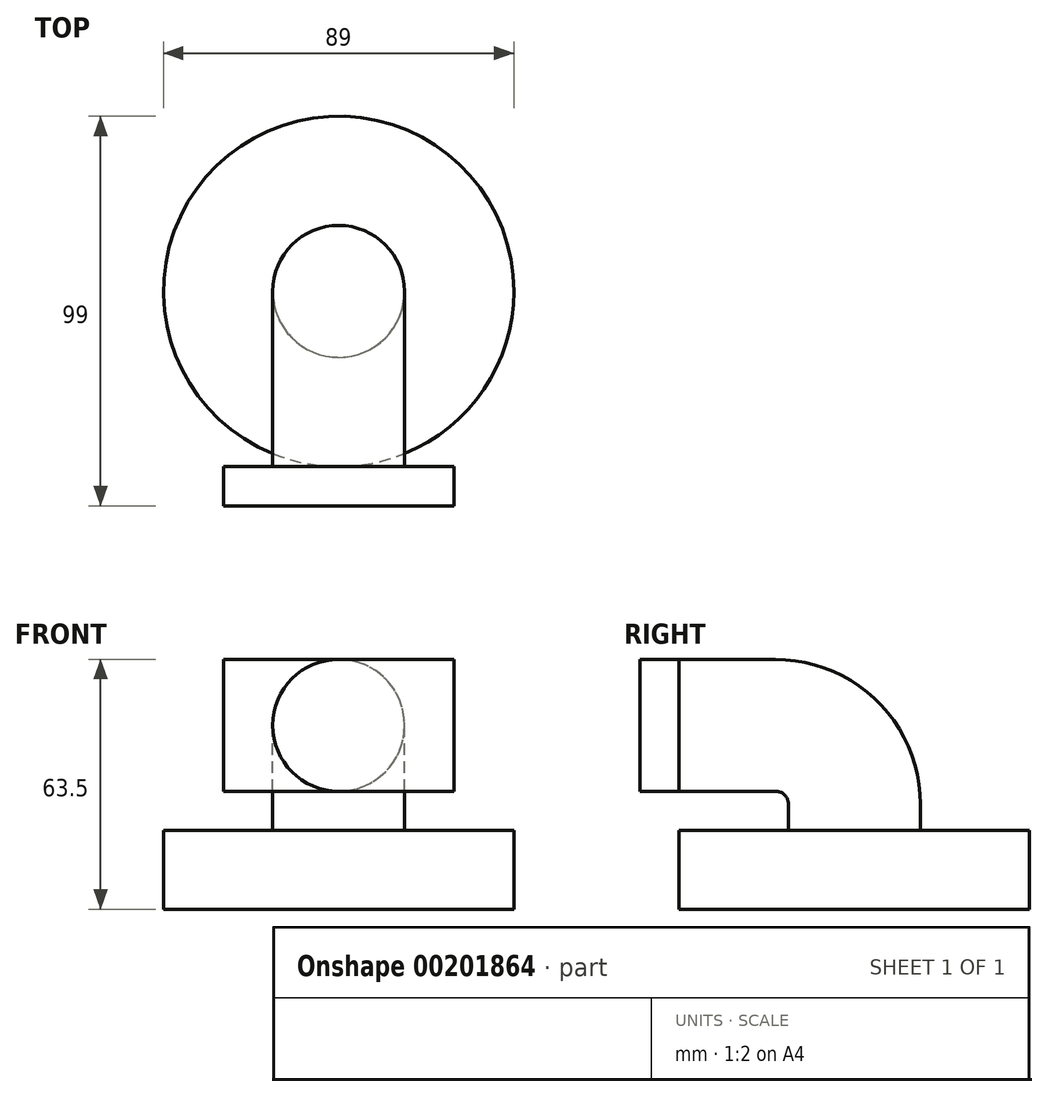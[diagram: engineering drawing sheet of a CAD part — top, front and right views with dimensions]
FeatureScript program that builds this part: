
annotation { "Feature Type Name" : "Feature", "Feature Type Description" : "" }
export const myFeature = defineFeature(function(context is Context, id is Id, definition is map)
    precondition{}
    {
        {
            var Q0;
            Q0=qCreatedBy(makeId("Top.planeOp"),FACE);
            var sketch = newSketch(context, id + "F0", { "sketchPlane" : qUnion([Q0])});
            skCircle(sketch, "E0", {"center": v(0, 0) * mm, "radius": 44.5 * mm});
            skSolve(sketch);
        }
        {
            var Q0;
            Q0=makeQuery(id+"F0.imprint","IMPRINT",FACE,{"disambiguationData":[TD([[makeQuery(id+"F0.imprint","IMPRINT",EDGE,{"derivedFrom":sQuery(id+"F0.wireOp",EDGE,"E0")}),1.0]])]});
            extrude(context, id + "F1", {"entities" : qUnion([Q0]), "depth" : 20 * mm, "offsetDistance" : 25 * mm});
        }
        {
            var Q0;
            Q0=qCreatedBy(makeId("Front.planeOp"),FACE);
            cPlane(context, id + "F2", {"entities" : qUnion([Q0]), "cplaneType" : CPlaneType.OFFSET, "offset" : (89 / 2) * mm, "width" : 150 * mm, "height" : 150 * mm});
        }
        {
            var Q0;
            Q0=makeQuery(id+"F1.opExtrude","CAP_FACE",FACE,{"disambiguationData":[OSD([sQuery(id+"F0.wireOp",EDGE,"E0")])],"isStart":false});
            var sketch = newSketch(context, id + "F3", { "sketchPlane" : qUnion([Q0])});
            skPoint(sketch, "E1", {"position": v(0, -44.5) * mm});
            skSolve(sketch);
        }
        {
            var Q0;
            Q0=qCreatedBy(id+"F2.planeOp",FACE);
            var sketch = newSketch(context, id + "F4", { "sketchPlane" : qUnion([Q0])});
            skLineSegment(sketch, "E2.bottom", {"start": v(29.25, 30) * mm, "end": v(-29.25, 30) * mm});
            skLineSegment(sketch, "E2.top", {"start": v(29.25, 63.5) * mm, "end": v(-29.25, 63.5) * mm});
            skLineSegment(sketch, "E2.left", {"start": v(29.25, 30) * mm, "end": v(29.25, 63.5) * mm});
            skLineSegment(sketch, "E2.right", {"start": v(-29.25, 30) * mm, "end": v(-29.25, 63.5) * mm});
            skPoint(sketch, "E2.middle", {"position": v(0, 46.75) * mm});
            skSolve(sketch);
        }
        {
            var Q0;
            Q0 = qSketchRegion(id + "F4", true);
            extrude(context, id + "F5", {"entities" : qUnion([Q0]), "depth" : 10 * mm, "offsetDistance" : 25 * mm});
        }
        {
            var Q0;
            Q0=makeQuery(id+"F3.imprint","IMPRINT",FACE,{"disambiguationData":[TD([[makeQuery(id+"F3.imprint","IMPRINT",EDGE,{"derivedFrom":makeQuery(id+"F1.opExtrude","CAP_EDGE",EDGE,{"disambiguationData":[OSD([sQuery(id+"F0.wireOp",EDGE,"E0")])],"isStart":false})}),1.0]])]});
            var sketch = newSketch(context, id + "F6", { "sketchPlane" : qUnion([Q0])});
            skPoint(sketch, "E3", {"position": v(0, 0) * mm});
            skSolve(sketch);
        }
        {
            var Q0;
            Q0=makeQuery(id+"F5.opExtrude","CAP_FACE",FACE,{"disambiguationData":[OSD([sQuery(id+"F4.wireOp",EDGE,"E2.bottom"),sQuery(id+"F4.wireOp",EDGE,"E2.top"),sQuery(id+"F4.wireOp",EDGE,"E2.left"),sQuery(id+"F4.wireOp",EDGE,"E2.right")])],"isStart":true});
            var sketch = newSketch(context, id + "F7", { "sketchPlane" : qUnion([Q0])});
            skCircle(sketch, "E4", {"center": v(0, 46.75) * mm, "radius": 16.75 * mm});
            skPoint(sketch, "E4.centerSnap0", {"position": v(29.25, 46.75) * mm});
            skPoint(sketch, "E4.centerSnap1", {"position": v(0, 63.5) * mm});
            skSolve(sketch);
        }
        {
            var Q0;
            Q0=qCreatedBy(makeId("Right.planeOp"),FACE);
            var sketch = newSketch(context, id + "F8", { "sketchPlane" : qUnion([Q0])});
            skPoint(sketch, "E5.0", {"position": v(-44.5, 46.75) * mm});
            skLineSegment(sketch, "E6", {"start": v(-44.5, 46.75) * mm, "end": v(-20, 46.75) * mm});
            skPoint(sketch, "E7.visualSharp", {"position": v(0, 46.75) * mm});
            skArc(sketch, "E7.filletArc", {"start": v(0, 26.75) * mm, "mid": v(-5.86, 40.9) * mm, "end": v(-20, 46.75) * mm});
            skPoint(sketch, "E8.0", {"position": v(0, 20) * mm});
            skLineSegment(sketch, "E9", {"start": v(0, 26.75) * mm, "end": v(0, 20) * mm});
            skSolve(sketch);
        }
        {
            var Q0;
            {var subQ0=sQuery(id+"F7.wireOp",EDGE,"E4");var subQ1=makeQuery(id+"F7.imprint","INTERSECT",VERTEX,{"derivedFrom":[makeQuery(id+"F5.opExtrude","CAP_EDGE",EDGE,{"disambiguationData":[OSD([sQuery(id+"F4.wireOp",EDGE,"E2.bottom")])],"isStart":true}),subQ0]});Q0=makeQuery(id+"F7.imprint","IMPRINT",FACE,{"disambiguationData":[TD([[makeQuery(id+"F7.imprint","IMPRINT",EDGE,{"disambiguationData":[TD([[subQ1,1.0]])],"derivedFrom":subQ0}),1.0]])]});}
            var Q1;
            Q1=sQuery(id+"F8.wireOp",EDGE,"E6");
            var Q2;
            Q2=sQuery(id+"F8.wireOp",EDGE,"E7.filletArc");
            var Q3;
            Q3=sQuery(id+"F8.wireOp",EDGE,"9CoemqA6-wfmC-Azzy-dYMY-l1sAoB2G5xHG");
            var Q4;
            Q4=sQuery(id+"F8.wireOp",EDGE,"E9");
            sweep(context, id + "F9", {"profiles" : qUnion([Q0]), "path" : qUnion([Q1, Q2, Q3, Q4])});
        }
    });
